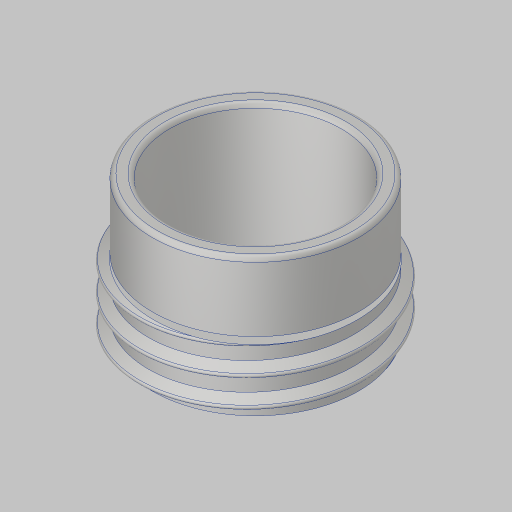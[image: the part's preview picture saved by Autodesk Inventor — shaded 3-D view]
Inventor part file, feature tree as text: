
AUTODESK INVENTOR PART (.ipt)
format: ipt  version: 2023.5 (Build 275446000, 446)  size: 419,840 bytes
history: native  units: in
note: dims shown in document units (in); Inventor stores cm internally (conversion verified against a paired STEP export)
features: sketch x5, extrude x4, helix x1, fillet x1, projected_geometry x1
ambient origin geometry x8: Origin, YZ Plane, XZ Plane, XY Plane, X Axis, Y Axis, Z Axis, Center Point
bodies: Solid1 (feature_tree)
feature tree (12):
  extrude  "Extrusion1"  Depth=1.0in TaperAngle=0.0deg
  helix  "Coil1"  [1 undecoded]
  extrude  "Extrusion2"  TaperAngle=0.0deg  [1 undecoded]
  extrude  "Extrusion3"  Depth=1.0in
  extrude  "Extrusion4"  Depth=0.0312in
  fillet  "Fillet1"  Radius=0.1in
  sketch  "Sketch1"  dims[d0=1.5in d1=1.0in d2=0.0in d19=0.015in]
  sketch  "Sketch2"  dims[d20=0.2in d21=1.0in d22=2.3622in d23=0.0in d24=90.0deg d25=90.0deg d26=0.0in d27=0.0in d28=0.0in d29=0.0in]
  sketch  "Sketch3"  dims[d30=1.0in d31=0.0in d32=1.25in]
  sketch  "Sketch4"  dims[d33=0.0in d34=0.0in d35=0.0312in d36=0.1in]
  sketch  "Sketch5"
  projected_geometry  "Project Cut Edges1"
note: 2 required parameter values undecoded (feature->parameter linkage not recoverable at this tier; creation-order binding heuristic only, values carry confidence <= 0.55)
